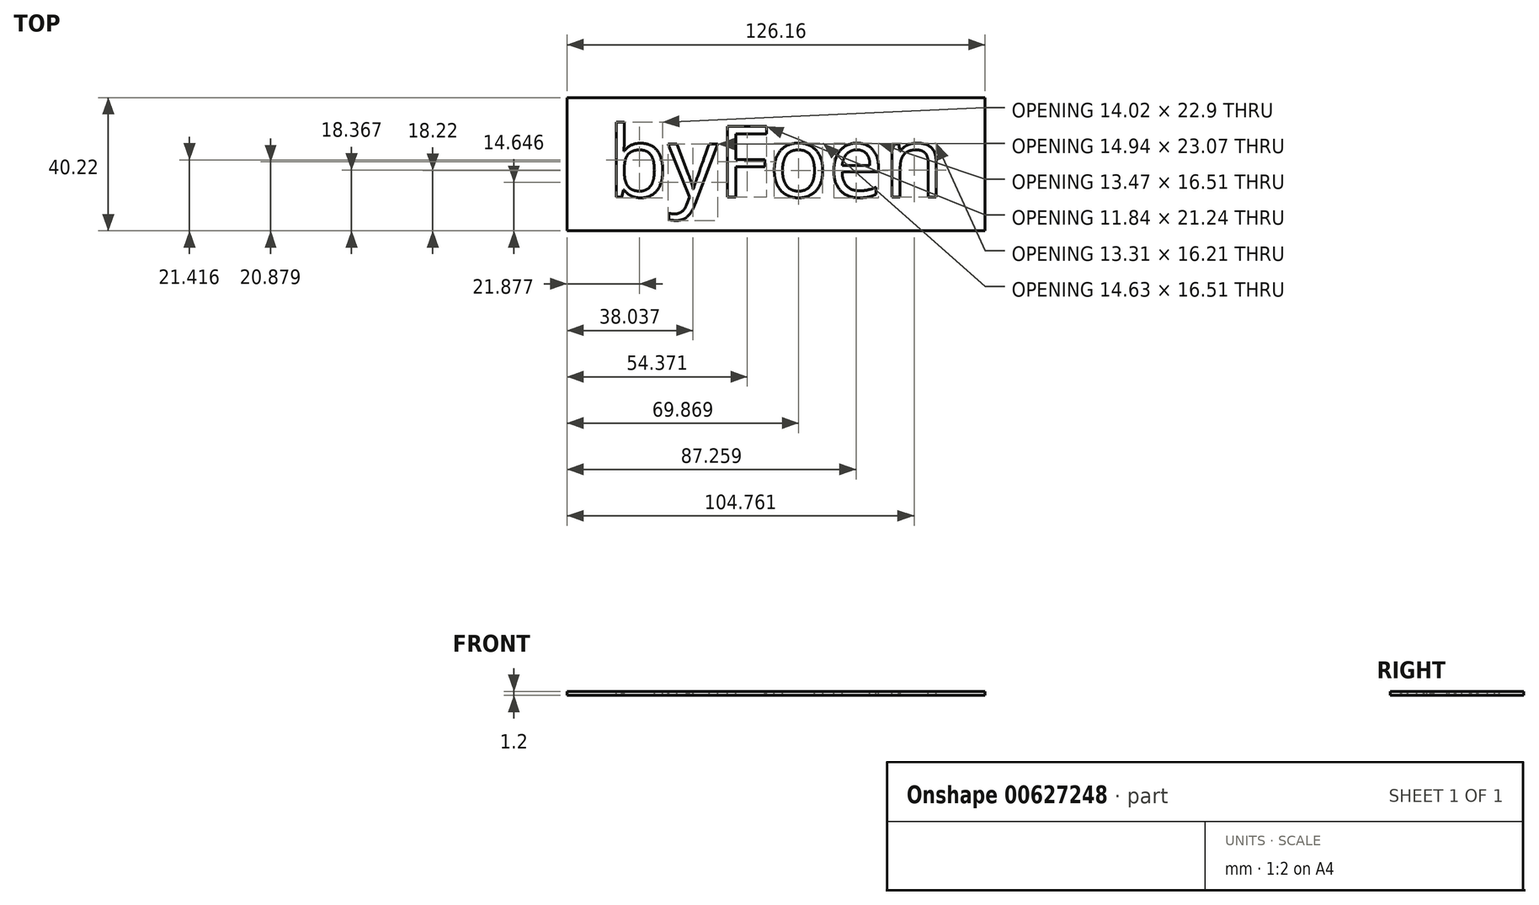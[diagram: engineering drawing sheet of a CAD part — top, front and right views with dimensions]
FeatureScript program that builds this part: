
annotation { "Feature Type Name" : "Feature", "Feature Type Description" : "" }
export const myFeature = defineFeature(function(context is Context, id is Id, definition is map)
    precondition{}
    {
        {
            var Q0;
            Q0=qCreatedBy(makeId("Top.planeOp"),FACE);
            var sketch = newSketch(context, id + "F0", { "sketchPlane" : qUnion([Q0])});
            skLineSegment(sketch, "E0.bottom", {"start": v(-63.08, 20.1) * mm, "end": v(63.08, 20.1) * mm});
            skLineSegment(sketch, "E0.top", {"start": v(-63.08, -20.1) * mm, "end": v(63.08, -20.1) * mm});
            skLineSegment(sketch, "E0.left", {"start": v(-63.08, 20.1) * mm, "end": v(-63.08, -20.1) * mm});
            skLineSegment(sketch, "E0.right", {"start": v(63.08, 20.1) * mm, "end": v(63.08, -20.1) * mm});
            skPoint(sketch, "E0.middle", {"position": v(0, 0) * mm});
            skSolve(sketch);
        }
        {
            var Q0;
            Q0=makeQuery(id+"F0.imprint","IMPRINT",FACE,{"disambiguationData":[TD([[makeQuery(id+"F0.imprint","IMPRINT",EDGE,{"derivedFrom":sQuery(id+"F0.wireOp",EDGE,"E0.bottom")}),-1.0]])]});
            extrude(context, id + "F1", {"entities" : qUnion([Q0]), "depth" : 1.2 * mm, "offsetDistance" : 25 * mm});
        }
        {
            var Q0;
            Q0=makeQuery(id+"F1.opExtrude","CAP_FACE",FACE,{"disambiguationData":[OSD([sQuery(id+"F0.wireOp",EDGE,"E0.bottom"),sQuery(id+"F0.wireOp",EDGE,"E0.top"),sQuery(id+"F0.wireOp",EDGE,"E0.left"),sQuery(id+"F0.wireOp",EDGE,"E0.right")])],"isStart":false});
            var sketch = newSketch(context, id + "F2", { "sketchPlane" : qUnion([Q0])});
            skText(sketch, "E1", { "text": "byFoen", "fontName": "OpenSans-Regular.ttf"});
            const initialGuessF2  = {"E1": [-0.05077, -0.00985, 1, 0, 0.02142]};
            skSetInitialGuess(sketch, initialGuessF2);
            skSolve(sketch);
        }
        {
            var Q0;
            Q0 = qSketchRegion(id + "F2", true);
            extrude(context, id + "F3", {"entities" : qUnion([Q0]), "operationType" : NewBodyOperationType.REMOVE, "endBound" : BoundingType.THROUGH_ALL, "oppositeDirection" : true, "depth" : 25 * mm, "offsetDistance" : 25 * mm});
        }
    });
